# Revit family: BISLEY_SystemFile_Combination_Units
name_source: partatom
category: Furniture
revit_build: Autodesk Revit 2018 (Build: 20180423_1000(x64)
units: mm (PartAtom-declared; Revit-internal decimal feet)

## family parameters
Always vertical = Yes
Cut with Voids When Loaded = No
OmniClass Number = 23.40.20.00
OmniClass Title = General Furniture and Specialties
Room Calculation Point = No
Shared = No
Work Plane-Based = No

## types (16) — shared parameters
Category = Furniture
Compliance Standards Certification = We recommend you clean your unit with warm water and a mild detergent solution. A damp cloth can be used to remove dust particles.
Depth = 470 mm  [stored 1.54199 ft]
Finish = Powder Coated
Manufacturer = BISLEY
Material = Steel
Product Information = Combination Unit
Range = SystemFile
Routine Maintenance = We recommend you clean your unit with warm water and a mild detergent solution. A damp cloth can be used to remove dust particles.
URL = www.bisley.com
Uniclass 2015 Code = PR_40_30_57
Uniclass2015Title = Shelves and Storage Units
Uniclass2015Version = V1.1
Warranty = 10 Years
feet dim = 65 mm  [stored 0.213255 ft]

## per-type parameters (varying)
| type | Bottom Flipper | Description | Doors | Drawer width1 | Drawer width2 | Height | Model Reference | Number of drawers | Tambour | Tambour width | TieBar Height | Top Flipper | Top Flipper height | Width |
| SYC08/34/1/2 | No | 1 x 419.1mm flipper, 2 drawers and counterbalance | No | 377 mm  [stored 1.23688 ft] | -377 mm | 1149 mm  [stored 3.76969 ft] | SYC08/34/1/2 | 2 | No | 5 | 610 mm | Yes | 414 mm  [stored 1.35827 ft] | 800 mm  [stored 2.62467 ft] |
| SYC08/43/1/3 | No | 1 x 381mm flipper, 3 drawers and counterbalance | No | 377 mm  [stored 1.23688 ft] | -377 mm | 1415 mm  [stored 4.64239 ft] | SYC08/43/1/3 | 3 | No | 5 | 913 mm | Yes | 377 mm  [stored 1.23688 ft] | 800 mm  [stored 2.62467 ft] |
| SYC08/50/2/3 | Yes | 2 x 304.8mm flippers, lateral rails, 3 drawers and counterbalance | No | 377 mm  [stored 1.23688 ft] | -377 mm | 1643 mm  [stored 5.39042 ft] | SYC08/50/2/3 | 3 | No | 5 | 913 mm | Yes | 301 mm  [stored 0.987533 ft] | 800 mm  [stored 2.62467 ft] |
| SYC08/2/3 | Yes | 2 x 381mm flippers, shelf and 3 drawers | No | 377 mm  [stored 1.23688 ft] | -377 mm | 1795 mm | SYC08/2/3 | 3 | No | 5 | 913 mm | Yes | 377 mm  [stored 1.23688 ft] | 800 mm  [stored 2.62467 ft] |
| SYC08/2/4 | Yes | 2 x 304.8 flippers, lateral rails and 4 drawers | No | 377 mm  [stored 1.23688 ft] | -377 mm | 1947 mm  [stored 6.3878 ft] | SYC08/2/4 | 4 | No | 5 | 1217 mm | Yes | 301 mm  [stored 0.987533 ft] | 800 mm  [stored 2.62467 ft] |
| SYC08/30D/3 | No | 762mm doors, 1 adjustable shelf and 3 drawers | Yes | 377 mm  [stored 1.23688 ft] | -377 mm | 1795 mm | SYC08/30D/3 | 3 | No | 5 | 913 mm | No | 150 mm | 800 mm  [stored 2.62467 ft] |
| SYC08/30T/3 | No | 762mm tambour, 1 adjustable shelf and 3 drawers | No | 377 mm  [stored 1.23688 ft] | -377 mm | 1795 mm | SYC08/30T/3 | 3 | Yes | 24 | 913 mm | No | 414 mm  [stored 1.35827 ft] | 800 mm  [stored 2.62467 ft] |
| SYC08/36D/3 | No | 914.4mm doors, 1 adjustable shelf and 3 drawers | Yes | 377 mm  [stored 1.23688 ft] | -377 mm | 1947 mm  [stored 6.3878 ft] |  | 3 | No | 5 | 913 mm | No | 414 mm  [stored 1.35827 ft] | 800 mm  [stored 2.62467 ft] |
| SYC10/34/1/2 | No | 1 x 419.1mm flipper, 2 drawers and counterbalance | No | 477 mm  [stored 1.56496 ft] | -477 mm | 1149 mm  [stored 3.76969 ft] | SYC10/34/1/2 | 2 | No | 5 | 610 mm | Yes | 414 mm  [stored 1.35827 ft] | 1000 mm  [stored 3.28084 ft] |
| SYC10/43/1/3 | No | 1 x 381mm flipper, 3 drawers and counterbalance | No | 477 mm  [stored 1.56496 ft] | -477 mm | 1415 mm  [stored 4.64239 ft] | SYC10/43/1/3 | 3 | No | 5 | 913 mm | Yes | 377 mm  [stored 1.23688 ft] | 1000 mm  [stored 3.28084 ft] |
| SYC10/50/2/3 | Yes | 2 x 304.8mm flippers, lateral rails, 3 drawers and counterbalance | No | 477 mm  [stored 1.56496 ft] | -477 mm | 1643 mm  [stored 5.39042 ft] | SYC10/50/2/3 | 3 | No | 5 | 913 mm | Yes | 301 mm  [stored 0.987533 ft] | 1000 mm  [stored 3.28084 ft] |
| SYC10/2/3 | Yes | 2 x 381mm flippers, shelf and 3 drawers | No | 477 mm  [stored 1.56496 ft] | -477 mm | 1795 mm | SYC10/2/3 | 3 | No | 5 | 913 mm | Yes | 377 mm  [stored 1.23688 ft] | 1000 mm  [stored 3.28084 ft] |
| SYC10/2/4 | Yes | 2 x 304.8 flippers, lateral rails and 4 drawers | No | 477 mm  [stored 1.56496 ft] | -477 mm | 1947 mm  [stored 6.3878 ft] | SYC10/2/4 | 4 | No | 5 | 1217 mm | Yes | 301 mm  [stored 0.987533 ft] | 1000 mm  [stored 3.28084 ft] |
| SYC10/30D/3 | No | 762mm doors, 1 adjustable shelf and 3 drawers | Yes | 477 mm  [stored 1.56496 ft] | -477 mm | 1795 mm | SYC10/30D/3 | 3 | No | 5 | 913 mm | No | 414 mm  [stored 1.35827 ft] | 1000 mm  [stored 3.28084 ft] |
| SYC10/30T/3 | No | 762mm tambour, 1 adjustable shelf and 3 drawers | No | 477 mm  [stored 1.56496 ft] | -477 mm | 1795 mm | SYC10/30T/3 | 3 | Yes | 31 | 913 mm | No | 414 mm  [stored 1.35827 ft] | 1000 mm  [stored 3.28084 ft] |
| SYC10/36D/3 | No | 914.4mm doors, 1 adjustable shelf and 3 drawers | Yes | 477 mm  [stored 1.56496 ft] | -477 mm | 1947 mm  [stored 6.3878 ft] | SYC10/36D/3 | 3 | No | 5 | 913 mm | No | 414 mm  [stored 1.35827 ft] | 1000 mm  [stored 3.28084 ft] |

note: [stored X ft] marks values corroborated as IEEE doubles in the binary element streams (Revit-internal decimal feet)

## geometry (parser evidence)
native form markers: Sweep x1
no freeform markers — native parametric forms only
